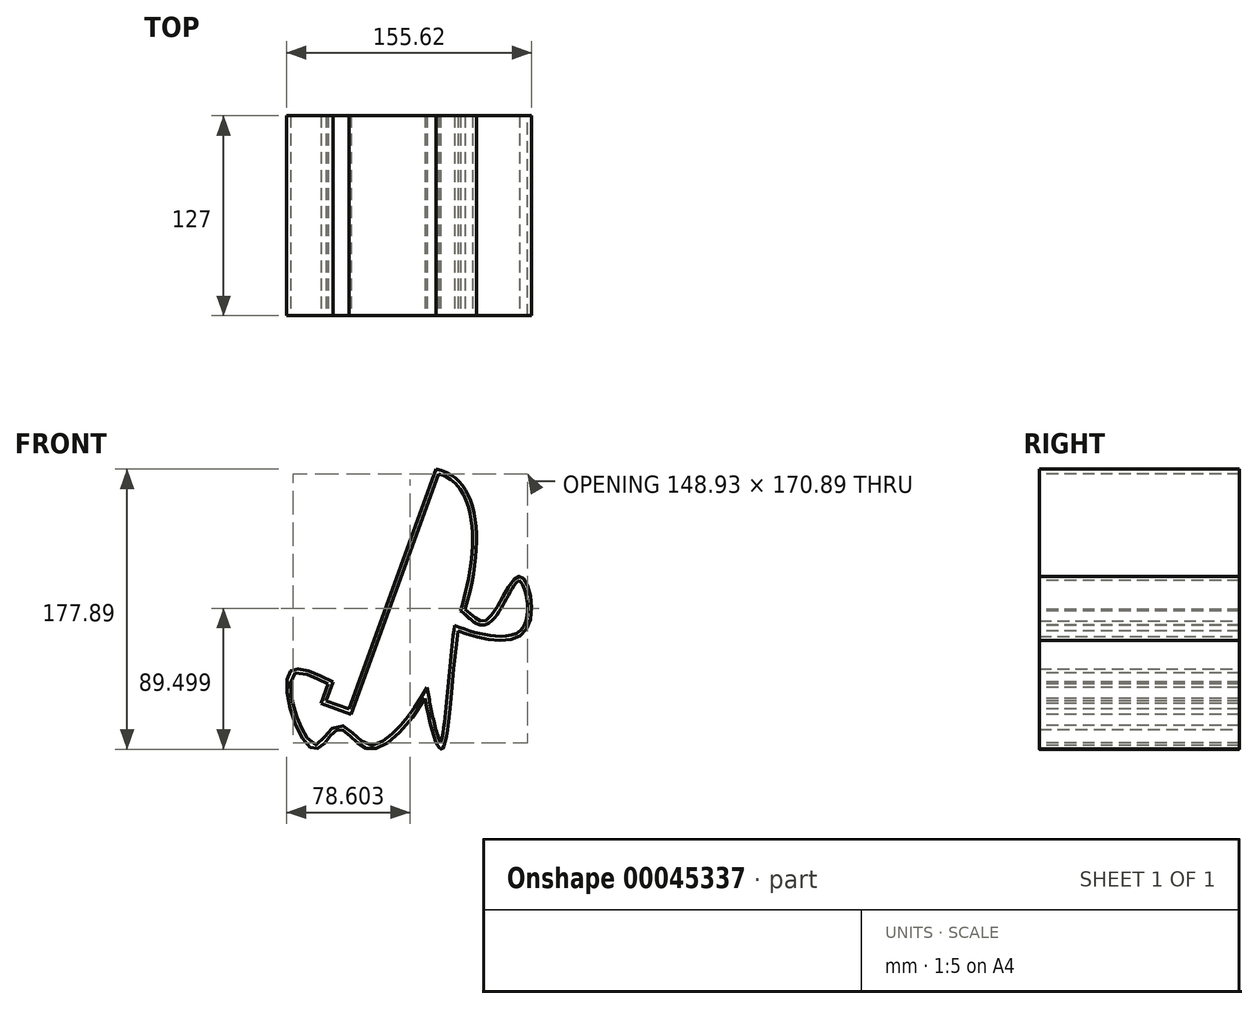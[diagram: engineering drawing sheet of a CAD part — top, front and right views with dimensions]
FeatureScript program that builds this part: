
annotation { "Feature Type Name" : "Feature", "Feature Type Description" : "" }
export const myFeature = defineFeature(function(context is Context, id is Id, definition is map)
    precondition{}
    {
        {
            var Q0;
            Q0=qCreatedBy(makeId("Front.planeOp"),FACE);
            var sketch = newSketch(context, id + "F0", { "sketchPlane" : qUnion([Q0])});
            skLineSegment(sketch, "E0.bottom", {"start": v(0, 0) * mm, "end": v(101.6, 0) * mm, "construction": true});
            skLineSegment(sketch, "E0.top", {"start": v(0, 177.8) * mm, "end": v(101.6, 177.8) * mm, "construction": true});
            skLineSegment(sketch, "E0.left", {"start": v(0, 0) * mm, "end": v(0, 177.8) * mm, "construction": true});
            skLineSegment(sketch, "E0.right", {"start": v(101.6, 0) * mm, "end": v(101.6, 177.8) * mm, "construction": true});
            skLineSegment(sketch, "E1", {"start": v(69.79, 177.8) * mm, "end": v(14.32, 25.4) * mm});
            skLineSegment(sketch, "E2", {"start": v(14.32, 25.4) * mm, "end": v(0, 30.61) * mm});
            skLineSegment(sketch, "E3", {"start": v(0, 30.61) * mm, "end": v(4.34, 42.55) * mm});
            skFitSpline(sketch, "E4", {"points": [v(4.34, 42.55) * mm, v(-24.26, 47.2) * mm, v(-7.77, 0) * mm, v(7.9, 12.56) * mm, v(27.3, 0) * mm, v(91.22, 100) * mm, v(69.79, 177.8) * mm], "startDerivative": vector(-278.99, 148.4) * mm, "endDerivative": vector(-346.6, 59.84) * mm});
            skFitSpline(sketch, "E5", {"points": [v(62.75, 32.07) * mm, v(73.07, 0) * mm, v(83.56, 74.98) * mm], "startDerivative": vector(21.9, -125.14) * mm, "endDerivative": vector(22.67, 189.61) * mm});
            skFitSpline(sketch, "E6", {"points": [v(83.56, 74.98) * mm, v(126.46, 74.98) * mm, v(122.8, 109.72) * mm, v(101.6, 81.85) * mm, v(88.2, 88.8) * mm], "startDerivative": vector(107.96, -41.2) * mm, "endDerivative": vector(-73.24, 55.9) * mm});
            skSolve(sketch);
        }
        {
            var Q0;
            {var subQ0=sQuery(id+"F0.wireOp",EDGE,"E5");Q0=makeQuery(id+"F0.imprint","IMPRINT",FACE,{"disambiguationData":[TD([[makeQuery(id+"F0.imprint","IMPRINT",EDGE,{"derivedFrom":subQ0}),1.0]])]});}
            var Q1;
            {var subQ4=sQuery(id+"F0.wireOp",EDGE,"E1");Q1=makeQuery(id+"F0.imprint","IMPRINT",FACE,{"disambiguationData":[TD([[makeQuery(id+"F0.imprint","IMPRINT",EDGE,{"derivedFrom":subQ4}),1.0]])]});}
            var Q2;
            {var subQ0=sQuery(id+"F0.wireOp",EDGE,"E6");Q2=makeQuery(id+"F0.imprint","IMPRINT",FACE,{"disambiguationData":[TD([[makeQuery(id+"F0.imprint","IMPRINT",EDGE,{"derivedFrom":subQ0}),1.0]])]});}
            extrude(context, id + "F1", {"entities" : qUnion([Q0, Q1, Q2]), "oppositeDirection" : true, "depth" : 127 * mm});
        }
        {
            var Q0;
            Q0=makeQuery(id+"F1.opExtrude","CAP_FACE",FACE,{"disambiguationData":[OSD([sQuery(id+"F0.wireOp",EDGE,"E1"),sQuery(id+"F0.wireOp",EDGE,"E2"),sQuery(id+"F0.wireOp",EDGE,"E3"),sQuery(id+"F0.wireOp",EDGE,"E4"),sQuery(id+"F0.wireOp",EDGE,"E5"),sQuery(id+"F0.wireOp",EDGE,"E6")])],"isStart":true});
            var Q1;
            Q1=makeQuery(id+"F1.opExtrude","CAP_FACE",FACE,{"disambiguationData":[OSD([sQuery(id+"F0.wireOp",EDGE,"E1"),sQuery(id+"F0.wireOp",EDGE,"E2"),sQuery(id+"F0.wireOp",EDGE,"E3"),sQuery(id+"F0.wireOp",EDGE,"E4"),sQuery(id+"F0.wireOp",EDGE,"E5"),sQuery(id+"F0.wireOp",EDGE,"E6")])],"isStart":false});
            shell(context, id + "F2", {"entities" : qUnion([Q0, Q1]), "thickness" : 2.54 * mm});
        }
    });
